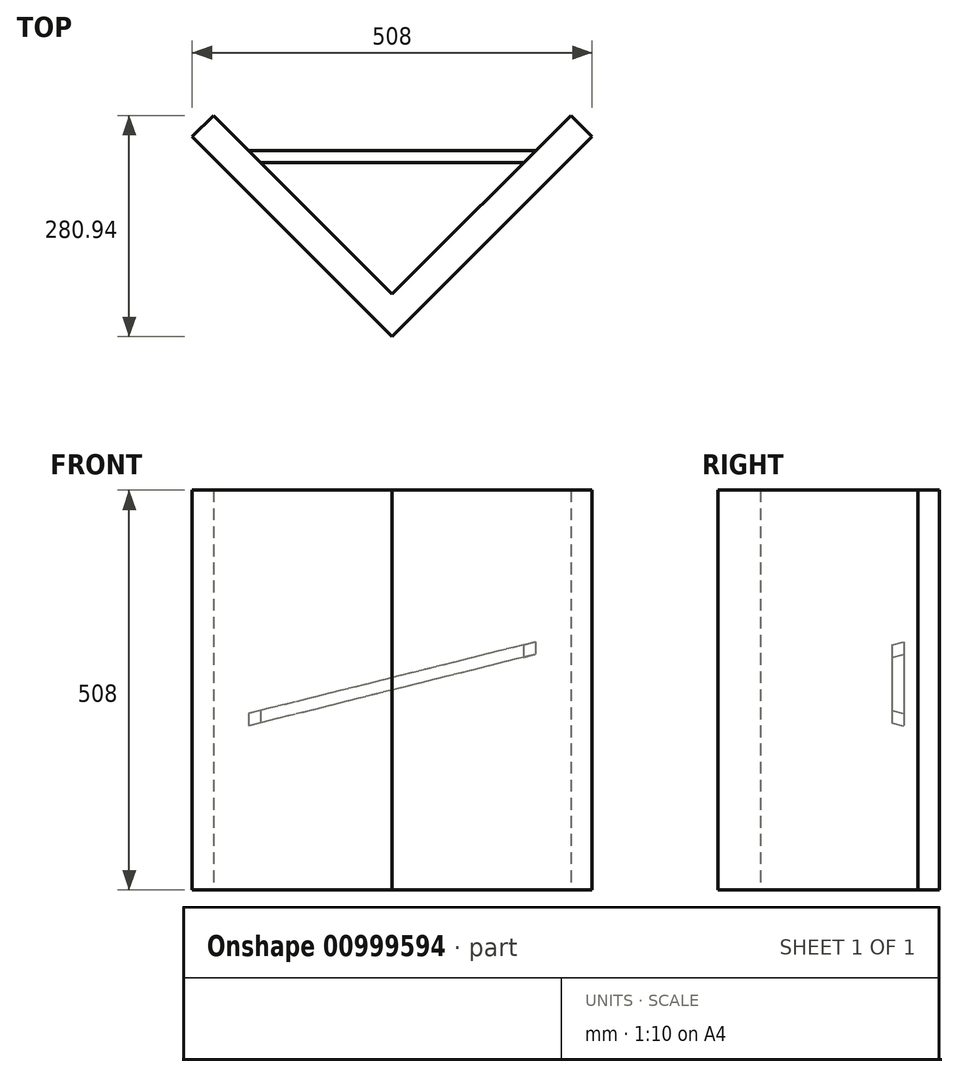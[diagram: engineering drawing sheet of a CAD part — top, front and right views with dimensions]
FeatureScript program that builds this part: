
annotation { "Feature Type Name" : "Feature", "Feature Type Description" : "" }
export const myFeature = defineFeature(function(context is Context, id is Id, definition is map)
    precondition{}
    {
        {
            var Q0;
            Q0=qCreatedBy(makeId("Top.planeOp"),FACE);
            var sketch = newSketch(context, id + "F0", { "sketchPlane" : qUnion([Q0])});
            skLineSegment(sketch, "E0", {"start": v(0, 0) * mm, "end": v(0, -44.55) * mm, "construction": true});
            skSolve(sketch);
        }
        {
            var Q0;
            Q0=qCreatedBy(makeId("Top.planeOp"),FACE);
            var Q1;
            Q1=sQuery(id+"F0.wireOp",EDGE,"E0");
            cPlane(context, id + "F1", {"entities" : qUnion([Q0, Q1]), "cplaneType" : CPlaneType.LINE_ANGLE, "offset" : 25.4 * mm, "angle" : 14 * degree, "width" : 152.4 * mm, "height" : 152.4 * mm});
        }
        {
            var Q0;
            Q0=qCreatedBy(id+"F1.planeOp",FACE);
            var sketch = newSketch(context, id + "F2", { "sketchPlane" : qUnion([Q0])});
            skLineSegment(sketch, "E1.bottom", {"start": v(217.57, 7.62) * mm, "end": v(-214.23, 7.62) * mm});
            skLineSegment(sketch, "E1.top", {"start": v(217.57, -7.62) * mm, "end": v(-214.23, -7.62) * mm});
            skLineSegment(sketch, "E1.left", {"start": v(217.57, 7.62) * mm, "end": v(217.57, -7.62) * mm});
            skLineSegment(sketch, "E1.right", {"start": v(-214.23, 7.62) * mm, "end": v(-214.23, -7.62) * mm});
            skPoint(sketch, "E1.middle", {"position": v(1.67, 0) * mm});
            skSolve(sketch);
        }
        {
            var Q0;
            Q0=makeQuery(id+"F2.imprint","IMPRINT",FACE,{"disambiguationData":[TD([[makeQuery(id+"F2.imprint","IMPRINT",EDGE,{"derivedFrom":sQuery(id+"F2.wireOp",EDGE,"E1.bottom")}),1.0]])]});
            extrude(context, id + "F3", {"entities" : qUnion([Q0]), "oppositeDirection" : true, "depth" : 15.24 * mm, "offsetDistance" : 25.4 * mm});
        }
        {
            var Q0;
            Q0=qCreatedBy(makeId("Top.planeOp"),FACE);
            var sketch = newSketch(context, id + "F4", { "sketchPlane" : qUnion([Q0])});
            skLineSegment(sketch, "E2", {"start": v(-227.06, 52.34) * mm, "end": v(0, -174.72) * mm});
            skLineSegment(sketch, "E3", {"start": v(0, -174.72) * mm, "end": v(227.06, 52.34) * mm});
            skLineSegment(sketch, "E4", {"start": v(227.06, 52.34) * mm, "end": v(254, 25.4) * mm});
            skLineSegment(sketch, "E5", {"start": v(254, 25.4) * mm, "end": v(0, -228.6) * mm});
            skLineSegment(sketch, "E6", {"start": v(0, -228.6) * mm, "end": v(-254, 25.4) * mm});
            skLineSegment(sketch, "E7", {"start": v(-254, 25.4) * mm, "end": v(-227.06, 52.34) * mm});
            skSolve(sketch);
        }
        {
            var Q0;
            Q0=makeQuery(id+"F4.imprint","IMPRINT",FACE,{"disambiguationData":[TD([[makeQuery(id+"F4.imprint","IMPRINT",EDGE,{"derivedFrom":sQuery(id+"F4.wireOp",EDGE,"E2")}),-1.0]])]});
            extrude(context, id + "F5", {"entities" : qUnion([Q0]), "operationType" : NewBodyOperationType.REMOVE, "endBound" : BoundingType.THROUGH_ALL, "oppositeDirection" : true, "depth" : 25.4 * mm, "offsetDistance" : 25.4 * mm});
        }
        {
            var Q0;
            Q0 = qSketchRegion(id + "F4", true);
            extrude(context, id + "F6", {"entities" : qUnion([Q0]), "operationType" : NewBodyOperationType.REMOVE, "endBound" : BoundingType.THROUGH_ALL, "depth" : 25.4 * mm, "offsetDistance" : 25.4 * mm});
        }
        {
            var Q0;
            Q0 = qSketchRegion(id + "F4", true);
            extrude(context, id + "F7", {"entities" : qUnion([Q0]), "operationType" : NewBodyOperationType.ADD, "endBound" : BoundingType.SYMMETRIC, "depth" : 508 * mm, "offsetDistance" : 25.4 * mm});
        }
    });
